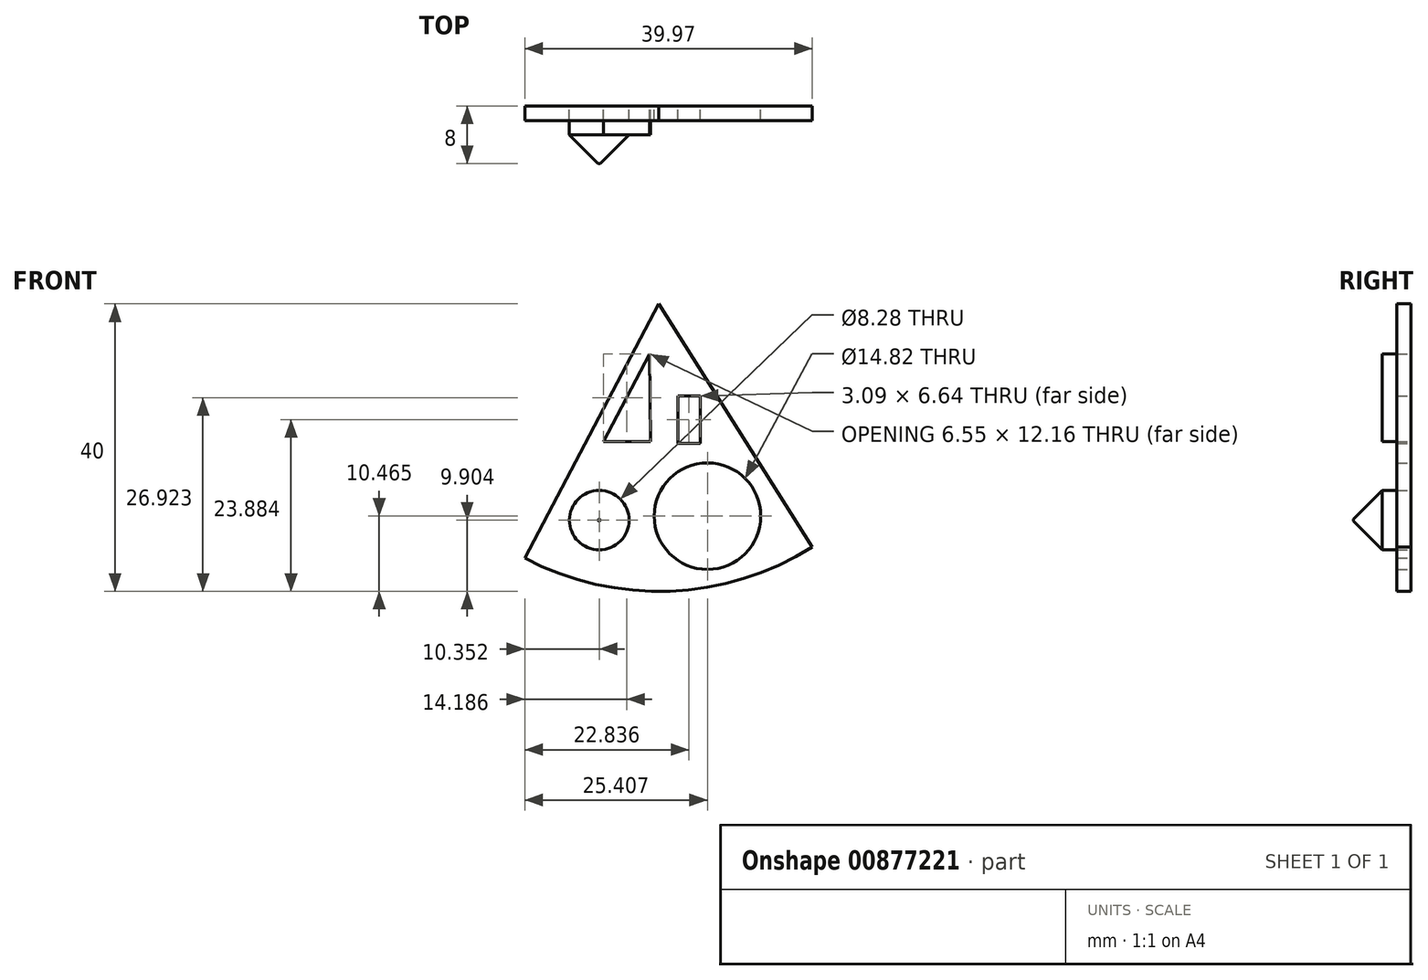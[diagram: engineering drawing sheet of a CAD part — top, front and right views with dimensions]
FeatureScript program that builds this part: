
annotation { "Feature Type Name" : "Feature", "Feature Type Description" : "" }
export const myFeature = defineFeature(function(context is Context, id is Id, definition is map)
    precondition{}
    {
        {
            var Q0;
            Q0=qCreatedBy(makeId("Front.planeOp"),FACE);
            var sketch = newSketch(context, id + "F0", { "sketchPlane" : qUnion([Q0])});
            skLineSegment(sketch, "E0", {"start": v(0, 0) * mm, "end": v(0, -24.36) * mm, "construction": true});
            skLineSegment(sketch, "E1", {"start": v(0, 20.41) * mm, "end": v(21.32, -13.43) * mm});
            skArc(sketch, "E2", {"start": v(-18.65, -14.98) * mm, "mid": v(1.54, -19.56) * mm, "end": v(21.32, -13.43) * mm});
            skLineSegment(sketch, "E3", {"start": v(-18.65, -14.98) * mm, "end": v(0, 20.41) * mm});
            skCircle(sketch, "E4", {"center": v(-8.3, -9.69) * mm, "radius": 4.14 * mm});
            skCircle(sketch, "E5", {"center": v(6.76, -9.13) * mm, "radius": 7.41 * mm});
            skLineSegment(sketch, "E6.bottom", {"start": v(2.64, 7.61) * mm, "end": v(5.73, 7.61) * mm});
            skLineSegment(sketch, "E6.top", {"start": v(2.64, 0.97) * mm, "end": v(5.73, 0.97) * mm});
            skLineSegment(sketch, "E6.left", {"start": v(2.64, 7.61) * mm, "end": v(2.64, 0.97) * mm});
            skLineSegment(sketch, "E6.right", {"start": v(5.73, 7.61) * mm, "end": v(5.73, 0.97) * mm});
            skLineSegment(sketch, "E7", {"start": v(-1.28, 13.41) * mm, "end": v(-7.74, 1.25) * mm});
            skLineSegment(sketch, "E8", {"start": v(-7.74, 1.25) * mm, "end": v(-1.2, 1.25) * mm});
            skLineSegment(sketch, "E9", {"start": v(-1.2, 1.25) * mm, "end": v(-1.28, 13.41) * mm});
            skSolve(sketch);
        }
        {
            var Q0;
            Q0 = qSketchRegion(id + "F0", true);
            extrude(context, id + "F1", {"entities" : qUnion([Q0]), "depth" : 2 * mm, "offsetDistance" : 25.4 * mm});
        }
        {
            var Q0;
            Q0=makeQuery(id+"F0.imprint","IMPRINT",FACE,{"disambiguationData":[TD([[makeQuery(id+"F0.imprint","IMPRINT",EDGE,{"derivedFrom":sQuery(id+"F0.wireOp",EDGE,"E7")}),1.0]])]});
            extrude(context, id + "F2", {"entities" : qUnion([Q0]), "depth" : 4 * mm, "offsetDistance" : 25.4 * mm});
        }
        {
            var Q0;
            Q0=makeQuery(id+"F0.imprint","IMPRINT",FACE,{"disambiguationData":[TD([[makeQuery(id+"F0.imprint","IMPRINT",EDGE,{"derivedFrom":sQuery(id+"F0.wireOp",EDGE,"E4")}),1.0]])]});
            extrude(context, id + "F3", {"entities" : qUnion([Q0]), "depth" : 8 * mm, "offsetDistance" : 25.4 * mm});
        }
        {
            var Q0;
            Q0=makeQuery(id+"F3.opExtrude","CAP_EDGE",EDGE,{"disambiguationData":[OSD([sQuery(id+"F0.wireOp",EDGE,"E4")])],"isStart":false});
            chamfer(context, id + "F4", {"entities" : qUnion([Q0]), "width" : 4 * mm, "tangentPropagation" : true});
        }
    });
